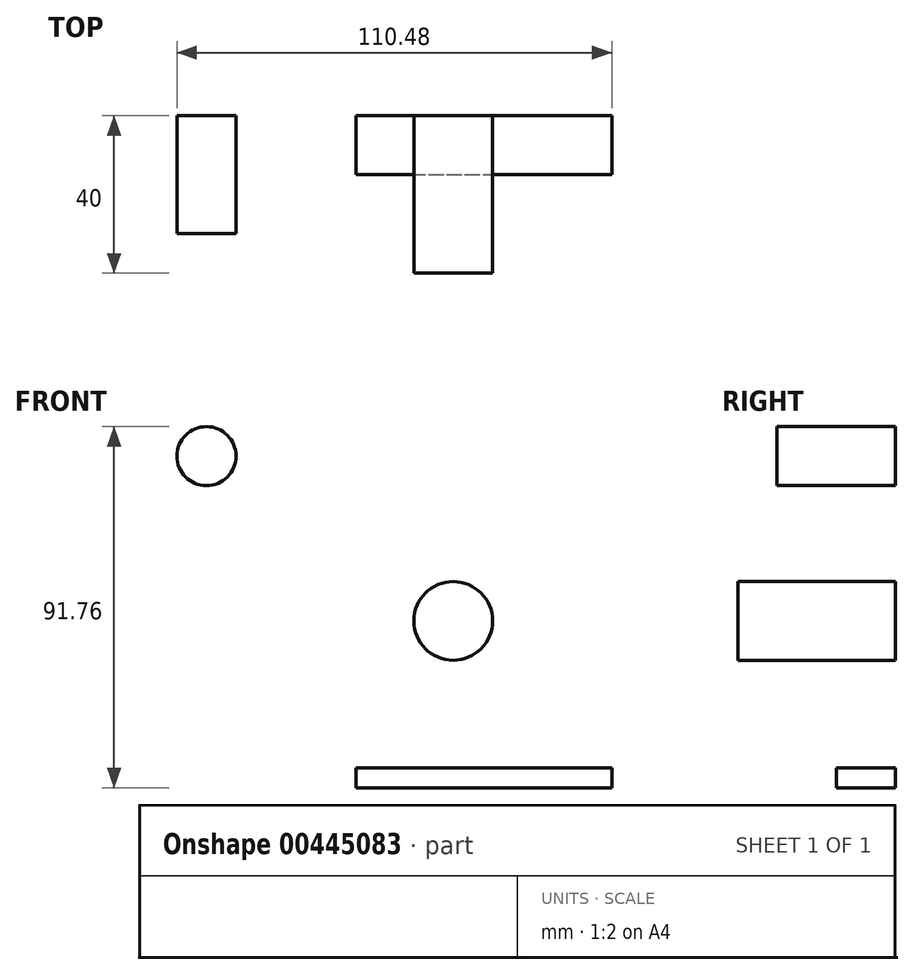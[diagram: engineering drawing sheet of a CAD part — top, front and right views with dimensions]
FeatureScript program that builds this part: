
annotation { "Feature Type Name" : "Feature", "Feature Type Description" : "" }
export const myFeature = defineFeature(function(context is Context, id is Id, definition is map)
    precondition{}
    {
        {
            var Q0;
            Q0=qCreatedBy(makeId("Front.planeOp"),FACE);
            var sketch = newSketch(context, id + "F0", { "sketchPlane" : qUnion([Q0])});
            skCircle(sketch, "E0", {"center": v(-62.68, 41.85) * mm, "radius": 7.5 * mm});
            skSolve(sketch);
        }
        {
            var Q0;
            Q0=makeQuery(id+"F0.imprint","IMPRINT",FACE,{"disambiguationData":[TD([[makeQuery(id+"F0.imprint","IMPRINT",EDGE,{"derivedFrom":sQuery(id+"F0.wireOp",EDGE,"E0")}),1.0]])]});
            extrude(context, id + "F1", {"entities" : qUnion([Q0]), "depth" : 30 * mm});
        }
        {
            var Q0;
            Q0=qCreatedBy(makeId("Front.planeOp"),FACE);
            var sketch = newSketch(context, id + "F2", { "sketchPlane" : qUnion([Q0])});
            skCircle(sketch, "E1", {"center": v(0, 0) * mm, "radius": 10 * mm});
            skSolve(sketch);
        }
        {
            var Q0;
            Q0 = qSketchRegion(id + "F2", true);
            extrude(context, id + "F3", {"entities" : qUnion([Q0]), "depth" : 40 * mm});
        }
        {
            var Q0;
            Q0=qCreatedBy(makeId("Front.planeOp"),FACE);
            var sketch = newSketch(context, id + "F4", { "sketchPlane" : qUnion([Q0])});
            skLineSegment(sketch, "E2.bottom", {"start": v(-24.7, -37.4) * mm, "end": v(40.3, -37.4) * mm});
            skLineSegment(sketch, "E2.top", {"start": v(-24.7, -42.4) * mm, "end": v(40.3, -42.4) * mm});
            skLineSegment(sketch, "E2.left", {"start": v(-24.7, -37.4) * mm, "end": v(-24.7, -42.4) * mm});
            skLineSegment(sketch, "E2.right", {"start": v(40.3, -37.4) * mm, "end": v(40.3, -42.4) * mm});
            skSolve(sketch);
        }
        {
            var Q0;
            Q0=makeQuery(id+"F4.imprint","IMPRINT",FACE,{"disambiguationData":[TD([[makeQuery(id+"F4.imprint","IMPRINT",EDGE,{"derivedFrom":sQuery(id+"F4.wireOp",EDGE,"E2.bottom")}),-1.0]])]});
            extrude(context, id + "F5", {"entities" : qUnion([Q0]), "depth" : 15 * mm});
        }
    });
